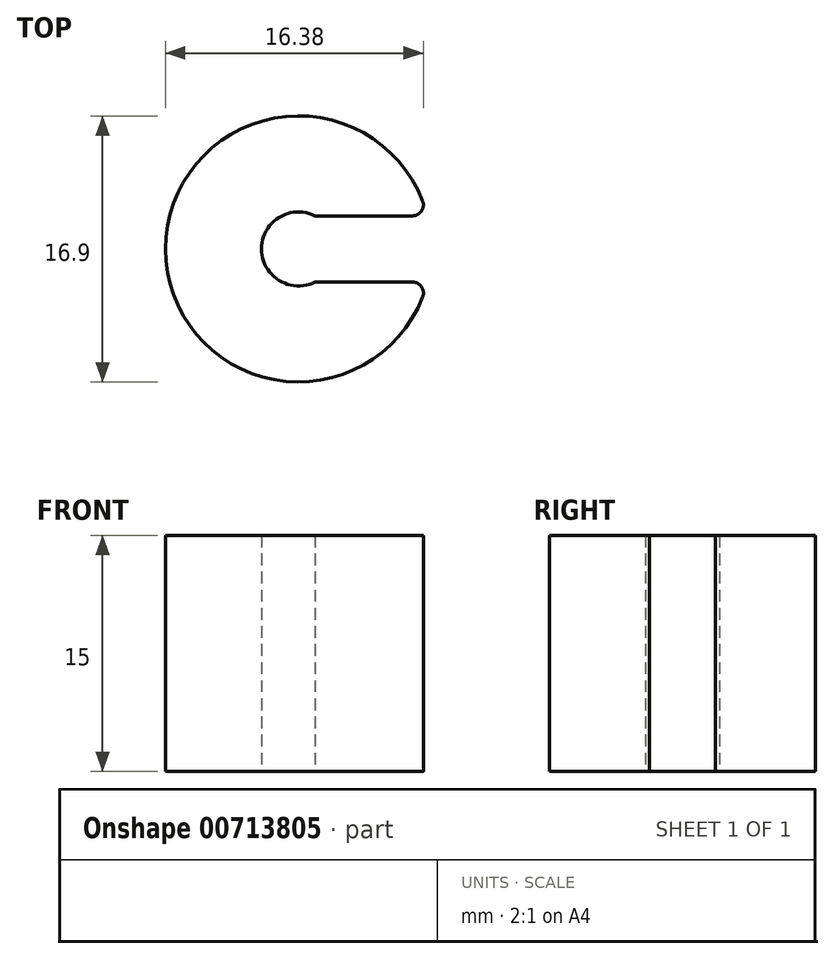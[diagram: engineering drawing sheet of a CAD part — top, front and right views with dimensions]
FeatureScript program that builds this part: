
annotation { "Feature Type Name" : "Feature", "Feature Type Description" : "" }
export const myFeature = defineFeature(function(context is Context, id is Id, definition is map)
    precondition{}
    {
        {
            var Q0;
            Q0=qCreatedBy(makeId("Top.planeOp"),FACE);
            var sketch = newSketch(context, id + "F0", { "sketchPlane" : qUnion([Q0])});
            skCircle(sketch, "E0", {"center": v(0, 0) * mm, "radius": 8.45 * mm});
            skCircle(sketch, "E1", {"center": v(0, 0) * mm, "radius": 2.35 * mm});
            skLineSegment(sketch, "E2", {"start": v(1.05, 2.1) * mm, "end": v(8.18, 2.1) * mm});
            skLineSegment(sketch, "E3", {"start": v(1.05, -2.1) * mm, "end": v(8.18, -2.1) * mm});
            skSolve(sketch);
        }
        {
            var Q0;
            {var subQ0=sQuery(id+"F0.wireOp",EDGE,"E2");Q0=makeQuery(id+"F0.imprint","IMPRINT",FACE,{"disambiguationData":[TD([[makeQuery(id+"F0.imprint","IMPRINT",EDGE,{"derivedFrom":subQ0}),1.0]])]});}
            extrude(context, id + "F1", {"entities" : qUnion([Q0]), "depth" : 15 * mm, "offsetDistance" : 25 * mm});
        }
        {
            var Q0;
            Q0=makeQuery(id+"F1.opExtrude","SWEPT_EDGE",EDGE,{"disambiguationData":[OSD([sQuery(id+"F0.wireOp",EDGE,"E0"),sQuery(id+"F0.wireOp",EDGE,"E2")])]});
            var Q1;
            Q1=makeQuery(id+"F1.opExtrude","SWEPT_EDGE",EDGE,{"disambiguationData":[OSD([sQuery(id+"F0.wireOp",EDGE,"E0"),sQuery(id+"F0.wireOp",EDGE,"E3")])]});
            fillet(context, id + "F2", {"entities" : qUnion([Q0, Q1]), "radius" : 0.7 * mm, "tangentPropagation" : true, "allowEdgeOverflow" : false});
        }
    });
